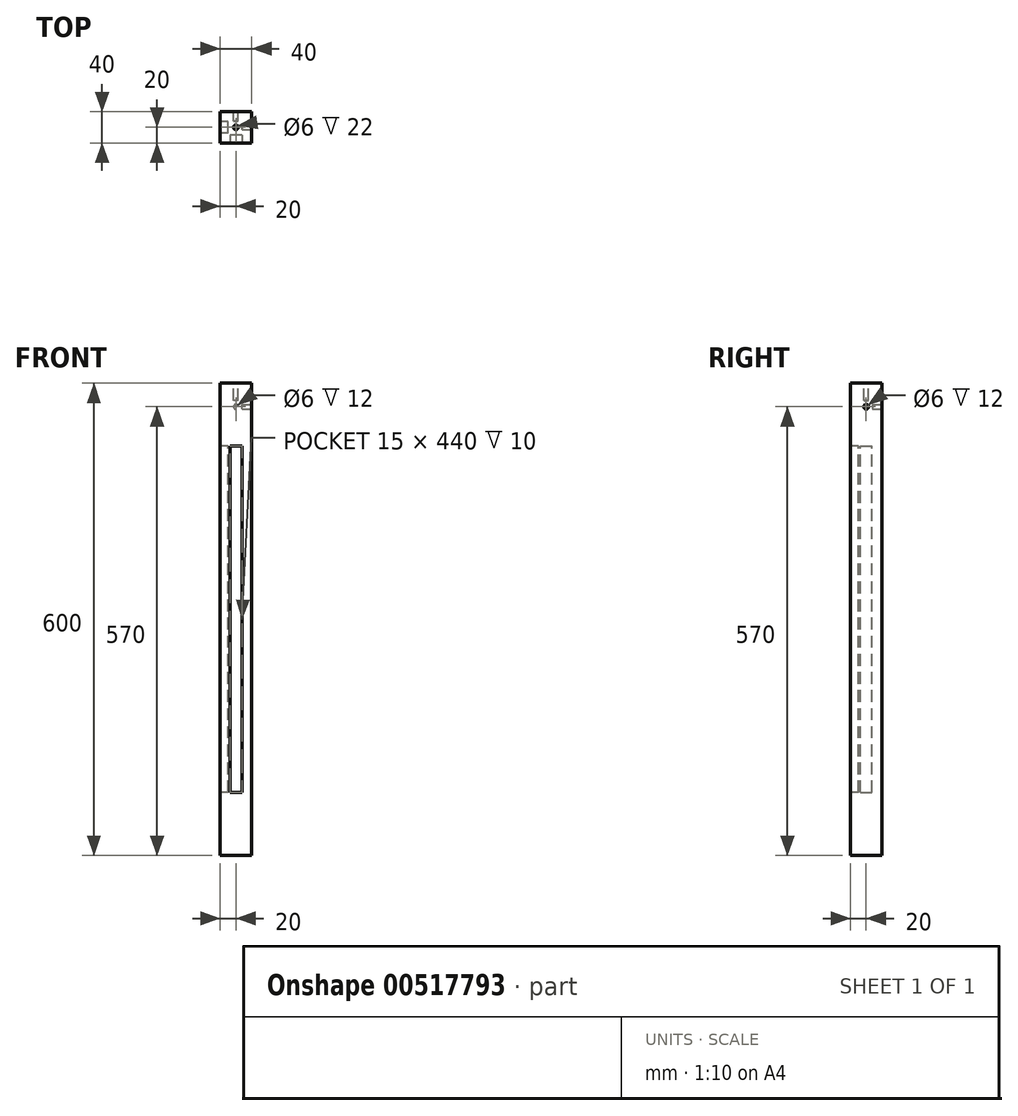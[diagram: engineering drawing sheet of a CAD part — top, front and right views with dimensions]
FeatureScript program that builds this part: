
annotation { "Feature Type Name" : "Feature", "Feature Type Description" : "" }
export const myFeature = defineFeature(function(context is Context, id is Id, definition is map)
    precondition{}
    {
        {
            var Q0;
            Q0=qCreatedBy(makeId("Top.planeOp"),FACE);
            var sketch = newSketch(context, id + "F0", { "sketchPlane" : qUnion([Q0])});
            skLineSegment(sketch, "E0.bottom", {"start": v(0, 0) * mm, "end": v(40, 0) * mm});
            skLineSegment(sketch, "E0.top", {"start": v(0, -40) * mm, "end": v(40, -40) * mm});
            skLineSegment(sketch, "E0.left", {"start": v(0, 0) * mm, "end": v(0, -40) * mm});
            skLineSegment(sketch, "E0.right", {"start": v(40, 0) * mm, "end": v(40, -40) * mm});
            skSolve(sketch);
        }
        {
            var Q0;
            Q0=makeQuery(id+"F0.imprint","IMPRINT",FACE,{"disambiguationData":[TD([[makeQuery(id+"F0.imprint","IMPRINT",EDGE,{"derivedFrom":sQuery(id+"F0.wireOp",EDGE,"E0.bottom")}),-1.0]])]});
            extrude(context, id + "F1", {"entities" : qUnion([Q0]), "depth" : 600 * mm, "offsetDistance" : 25 * mm});
        }
        {
            var Q0;
            Q0=makeQuery(id+"F1.opExtrude","SWEPT_FACE",FACE,{"disambiguationData":[OSD([sQuery(id+"F0.wireOp",EDGE,"E0.right")])]});
            var sketch = newSketch(context, id + "F2", { "sketchPlane" : qUnion([Q0])});
            skCircle(sketch, "E1", {"center": v(-20, 570) * mm, "radius": 3 * mm});
            skPoint(sketch, "E1.centerSnap0", {"position": v(-20, 600) * mm});
            skSolve(sketch);
        }
        {
            var Q0;
            Q0=makeQuery(id+"F2.imprint","IMPRINT",FACE,{"disambiguationData":[TD([[makeQuery(id+"F2.imprint","IMPRINT",EDGE,{"derivedFrom":sQuery(id+"F2.wireOp",EDGE,"E1")}),1.0]])]});
            var Q1;
            Q1=sQuery(id+"F2.wireOp",EDGE,"E1");
            extrude(context, id + "F3", {"entities" : qUnion([Q0]), "operationType" : NewBodyOperationType.REMOVE, "surfaceEntities" : qUnion([Q1]), "oppositeDirection" : true, "depth" : 12 * mm, "offsetDistance" : 25 * mm});
        }
        {
            var Q0;
            Q0=makeQuery(id+"F1.opExtrude","SWEPT_FACE",FACE,{"disambiguationData":[OSD([sQuery(id+"F0.wireOp",EDGE,"E0.bottom")])]});
            var sketch = newSketch(context, id + "F4", { "sketchPlane" : qUnion([Q0])});
            skCircle(sketch, "E2", {"center": v(-20, 570) * mm, "radius": 3 * mm});
            skPoint(sketch, "E2.centerSnap0", {"position": v(-20, 600) * mm});
            skSolve(sketch);
        }
        {
            var Q0;
            Q0=makeQuery(id+"F4.imprint","IMPRINT",FACE,{"disambiguationData":[TD([[makeQuery(id+"F4.imprint","IMPRINT",EDGE,{"derivedFrom":sQuery(id+"F4.wireOp",EDGE,"E2")}),1.0]])]});
            var Q1;
            Q1=sQuery(id+"F4.wireOp",EDGE,"E2");
            extrude(context, id + "F5", {"entities" : qUnion([Q0]), "operationType" : NewBodyOperationType.REMOVE, "surfaceEntities" : qUnion([Q1]), "oppositeDirection" : true, "depth" : 12 * mm, "offsetDistance" : 25 * mm});
        }
        {
            var Q0;
            Q0=makeQuery(id+"F1.opExtrude","CAP_FACE",FACE,{"disambiguationData":[OSD([sQuery(id+"F0.wireOp",EDGE,"E0.bottom"),sQuery(id+"F0.wireOp",EDGE,"E0.top"),sQuery(id+"F0.wireOp",EDGE,"E0.left"),sQuery(id+"F0.wireOp",EDGE,"E0.right")])],"isStart":false});
            var sketch = newSketch(context, id + "F6", { "sketchPlane" : qUnion([Q0])});
            skCircle(sketch, "E3", {"center": v(20, -20) * mm, "radius": 3 * mm});
            skPoint(sketch, "E3.centerSnap0", {"position": v(0, -20) * mm});
            skPoint(sketch, "E3.centerSnap1", {"position": v(20, 0) * mm});
            skSolve(sketch);
        }
        {
            var Q0;
            Q0=makeQuery(id+"F6.imprint","IMPRINT",FACE,{"disambiguationData":[TD([[makeQuery(id+"F6.imprint","IMPRINT",EDGE,{"derivedFrom":sQuery(id+"F6.wireOp",EDGE,"E3")}),1.0]])]});
            extrude(context, id + "F7", {"entities" : qUnion([Q0]), "operationType" : NewBodyOperationType.REMOVE, "oppositeDirection" : true, "depth" : 22 * mm, "offsetDistance" : 25 * mm});
        }
        {
            var Q0;
            Q0=makeQuery(id+"F1.opExtrude","SWEPT_FACE",FACE,{"disambiguationData":[OSD([sQuery(id+"F0.wireOp",EDGE,"E0.top")])]});
            var sketch = newSketch(context, id + "F8", { "sketchPlane" : qUnion([Q0])});
            skLineSegment(sketch, "E4.bottom", {"start": v(27.5, 80) * mm, "end": v(12.5, 80) * mm});
            skLineSegment(sketch, "E4.top", {"start": v(27.5, 520) * mm, "end": v(12.5, 520) * mm});
            skLineSegment(sketch, "E4.left", {"start": v(27.5, 80) * mm, "end": v(27.5, 520) * mm});
            skLineSegment(sketch, "E4.right", {"start": v(12.5, 80) * mm, "end": v(12.5, 520) * mm});
            skPoint(sketch, "E4.middle", {"position": v(20, 300) * mm});
            skPoint(sketch, "E4.middle.positionSnap0", {"position": v(0, 300) * mm});
            skPoint(sketch, "E4.middle.positionSnap1", {"position": v(20, 600) * mm});
            skPoint(sketch, "E4.centerSnap0", {"position": v(0, 300) * mm});
            skPoint(sketch, "E4.centerSnap1", {"position": v(20, 600) * mm});
            skSolve(sketch);
        }
        {
            var Q0;
            Q0=makeQuery(id+"F8.imprint","IMPRINT",FACE,{"disambiguationData":[TD([[makeQuery(id+"F8.imprint","IMPRINT",EDGE,{"derivedFrom":sQuery(id+"F8.wireOp",EDGE,"E4.bottom")}),-1.0]])]});
            extrude(context, id + "F9", {"entities" : qUnion([Q0]), "operationType" : NewBodyOperationType.REMOVE, "oppositeDirection" : true, "depth" : 10 * mm, "offsetDistance" : 25 * mm});
        }
        {
            var Q0;
            Q0=makeQuery(id+"F1.opExtrude","SWEPT_FACE",FACE,{"disambiguationData":[OSD([sQuery(id+"F0.wireOp",EDGE,"E0.left")])]});
            var sketch = newSketch(context, id + "F10", { "sketchPlane" : qUnion([Q0])});
            skLineSegment(sketch, "E5.bottom", {"start": v(27.5, 80) * mm, "end": v(12.5, 80) * mm});
            skLineSegment(sketch, "E5.top", {"start": v(27.5, 520) * mm, "end": v(12.5, 520) * mm});
            skLineSegment(sketch, "E5.left", {"start": v(27.5, 80) * mm, "end": v(27.5, 520) * mm});
            skLineSegment(sketch, "E5.right", {"start": v(12.5, 80) * mm, "end": v(12.5, 520) * mm});
            skPoint(sketch, "E5.middle", {"position": v(20, 300) * mm});
            skPoint(sketch, "E5.middle.positionSnap0", {"position": v(0, 300) * mm});
            skPoint(sketch, "E5.middle.positionSnap1", {"position": v(20, 600) * mm});
            skPoint(sketch, "E5.centerSnap0", {"position": v(0, 300) * mm});
            skPoint(sketch, "E5.centerSnap1", {"position": v(20, 600) * mm});
            skSolve(sketch);
        }
        {
            var Q0;
            Q0=makeQuery(id+"F10.imprint","IMPRINT",FACE,{"disambiguationData":[TD([[makeQuery(id+"F10.imprint","IMPRINT",EDGE,{"derivedFrom":sQuery(id+"F10.wireOp",EDGE,"E5.bottom")}),-1.0]])]});
            extrude(context, id + "F11", {"entities" : qUnion([Q0]), "operationType" : NewBodyOperationType.REMOVE, "oppositeDirection" : true, "depth" : 10 * mm, "offsetDistance" : 25 * mm});
        }
    });
